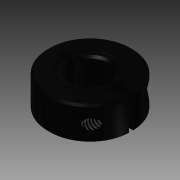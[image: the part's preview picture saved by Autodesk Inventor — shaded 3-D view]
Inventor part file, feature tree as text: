
AUTODESK INVENTOR PART (.ipt)
format: ipt  version: 2014 (Build 180170000, 170)  size: 386,560 bytes
history: native  units: mm
features: sketch x3, hole x2, other x2, surface_op x1, thread x1, extrude x1, projected_geometry x1
ambient origin geometry x8: Origin, YZ Plane, XZ Plane, XY Plane, X Axis, Y Axis, Z Axis, Center Point
bodies: Solid1 (feature_tree)
feature tree (11):
  surface_op  "Stitch Surface1"
  thread  "Thread1"  [1 undecoded]
  hole  "Hole1"  [1 undecoded]
  extrude  "Extrusion1"  [1 undecoded]
  hole  "Hole2"  [1 undecoded]
  sketch  "Sketch1"  dims[d2=3.797mm d3=6.0mm d4=12.7mm d5=2.362mm d6=14.3117mm d7=8.0mm d8=20.594885mm d9=9.25mm d10=0.0mm]
  sketch  "Sketch2"  dims[d11=2.642mm d12=10.0mm d13=12.7mm d14=2.362mm d15=14.3117mm d16=8.0mm d17=20.594885mm]
  sketch  "Sketch3"
  projected_geometry  "Projected Loop1"
  other  "Composite1"
  other  "Srf1"
note: 4 required parameter values undecoded (feature->parameter linkage not recoverable at this tier; creation-order binding heuristic only, values carry confidence <= 0.55)
